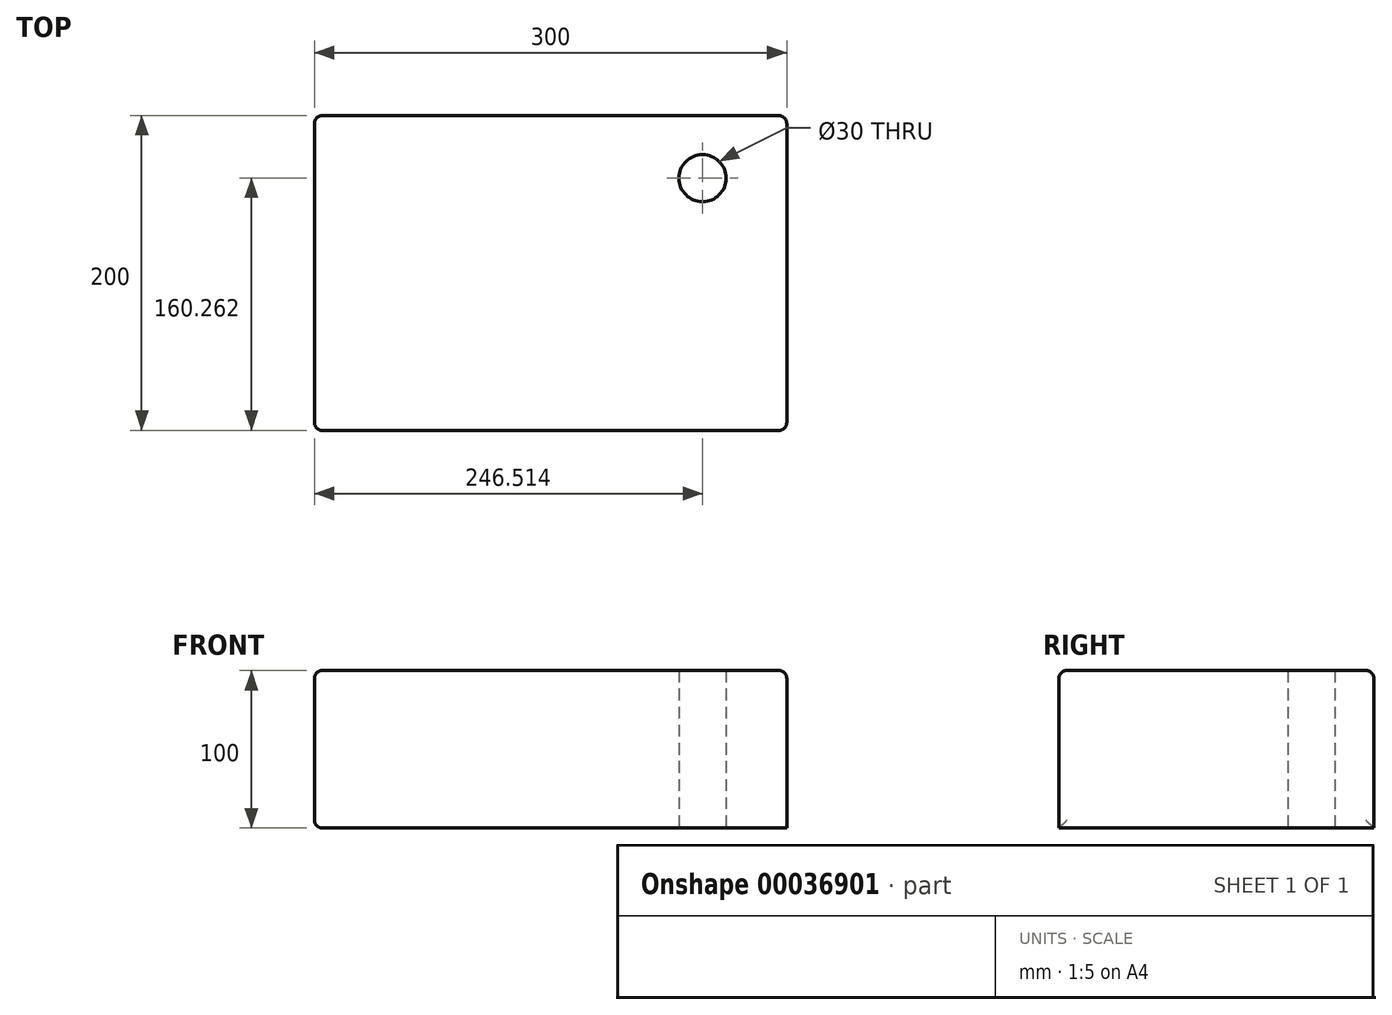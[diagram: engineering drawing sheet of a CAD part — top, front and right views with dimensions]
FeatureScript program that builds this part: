
annotation { "Feature Type Name" : "Feature", "Feature Type Description" : "" }
export const myFeature = defineFeature(function(context is Context, id is Id, definition is map)
    precondition{}
    {
        {
            var Q0;
            Q0=qCreatedBy(makeId("Top.planeOp"),FACE);
            var sketch = newSketch(context, id + "F0", { "sketchPlane" : qUnion([Q0])});
            skLineSegment(sketch, "E0.bottom", {"start": v(-148.74, 109.33) * mm, "end": v(151.26, 109.33) * mm});
            skLineSegment(sketch, "E0.top", {"start": v(-148.74, -90.67) * mm, "end": v(151.26, -90.67) * mm});
            skLineSegment(sketch, "E0.left", {"start": v(-148.74, 109.33) * mm, "end": v(-148.74, -90.67) * mm});
            skLineSegment(sketch, "E0.right", {"start": v(151.26, 109.33) * mm, "end": v(151.26, -90.67) * mm});
            skCircle(sketch, "E1", {"center": v(97.77, 69.6) * mm, "radius": 15 * mm});
            skLineSegment(sketch, "E2", {"start": v(-96.44, -29.41) * mm, "end": v(-102.05, -18.56) * mm});
            skLineSegment(sketch, "E3", {"start": v(-102.05, -18.56) * mm, "end": v(-98.68, -9.2) * mm});
            skLineSegment(sketch, "E4", {"start": v(-98.68, -9.2) * mm, "end": v(-92.32, -3.2) * mm});
            skLineSegment(sketch, "E5", {"start": v(-92.32, -3.2) * mm, "end": v(-79.97, -3.58) * mm});
            skLineSegment(sketch, "E6", {"start": v(-79.97, -3.58) * mm, "end": v(-72.1, -11.82) * mm});
            skLineSegment(sketch, "E7", {"start": v(-72.1, -11.82) * mm, "end": v(-57.88, -30.16) * mm});
            skLineSegment(sketch, "E8", {"start": v(-57.88, -30.16) * mm, "end": v(-30.93, -25.3) * mm});
            skLineSegment(sketch, "E9", {"start": v(-30.93, -25.3) * mm, "end": v(-21.2, -11.07) * mm});
            skLineSegment(sketch, "E10", {"start": v(-21.2, -11.07) * mm, "end": v(43.94, -61.6) * mm});
            skLineSegment(sketch, "E11", {"start": v(43.94, -61.6) * mm, "end": v(-60.5, -63.1) * mm});
            skLineSegment(sketch, "E12", {"start": v(-60.5, -63.1) * mm, "end": v(-96.44, -28.66) * mm});
            skSolve(sketch);
        }
        {
            var Q0;
            Q0=makeQuery(id+"F0.imprint","IMPRINT",FACE,{"disambiguationData":[TD([[makeQuery(id+"F0.imprint","IMPRINT",EDGE,{"derivedFrom":sQuery(id+"F0.wireOp",EDGE,"E0.bottom")}),-1.0]])]});
            extrude(context, id + "F1", {"entities" : qUnion([Q0]), "depth" : 100 * mm});
        }
        {
            var Q0;
            Q0=makeQuery(id+"F1.opExtrude","SWEPT_EDGE",EDGE,{"disambiguationData":[OSD([sQuery(id+"F0.wireOp",EDGE,"E0.bottom"),sQuery(id+"F0.wireOp",EDGE,"E0.left")])]});
            var Q1;
            Q1=makeQuery(id+"F1.opExtrude","SWEPT_EDGE",EDGE,{"disambiguationData":[OSD([sQuery(id+"F0.wireOp",EDGE,"E0.bottom"),sQuery(id+"F0.wireOp",EDGE,"E0.right")])]});
            var Q2;
            Q2=makeQuery(id+"F1.opExtrude","CAP_EDGE",EDGE,{"disambiguationData":[OSD([sQuery(id+"F0.wireOp",EDGE,"E0.bottom")])],"isStart":false});
            var Q3;
            Q3=makeQuery(id+"F1.opExtrude","CAP_EDGE",EDGE,{"disambiguationData":[OSD([sQuery(id+"F0.wireOp",EDGE,"E0.right")])],"isStart":false});
            var Q4;
            Q4=makeQuery(id+"F1.opExtrude","CAP_EDGE",EDGE,{"disambiguationData":[OSD([sQuery(id+"F0.wireOp",EDGE,"E0.left")])],"isStart":false});
            var Q5;
            Q5=makeQuery(id+"F1.opExtrude","CAP_EDGE",EDGE,{"disambiguationData":[OSD([sQuery(id+"F0.wireOp",EDGE,"E0.top")])],"isStart":false});
            var Q6;
            Q6=makeQuery(id+"F1.opExtrude","SWEPT_FACE",FACE,{"disambiguationData":[OSD([sQuery(id+"F0.wireOp",EDGE,"E0.left")])]});
            var Q7;
            Q7=makeQuery(id+"F1.opExtrude","SWEPT_EDGE",EDGE,{"disambiguationData":[OSD([sQuery(id+"F0.wireOp",EDGE,"E0.top"),sQuery(id+"F0.wireOp",EDGE,"E0.left")])]});
            var Q8;
            Q8=makeQuery(id+"F1.opExtrude","SWEPT_EDGE",EDGE,{"disambiguationData":[OSD([sQuery(id+"F0.wireOp",EDGE,"E0.top"),sQuery(id+"F0.wireOp",EDGE,"E0.right")])]});
            fillet(context, id + "F2", {"entities" : qUnion([Q0, Q1, Q2, Q3, Q4, Q5, Q6, Q7, Q8]), "radius" : 5 * mm, "tangentPropagation" : true, "allowEdgeOverflow" : false});
        }
    });
